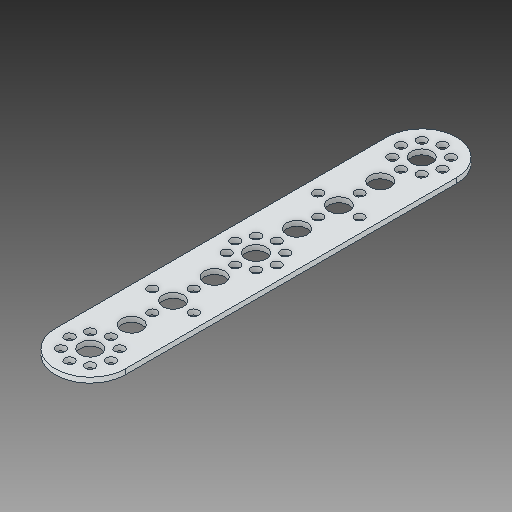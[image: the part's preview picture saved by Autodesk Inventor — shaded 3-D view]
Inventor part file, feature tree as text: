
AUTODESK INVENTOR PART (.ipt)
format: ipt  version: 2018 (Build 220112000, 112)  size: 172,032 bytes
history: native  units: in
note: dims shown in document units (in); Inventor stores cm internally (conversion verified against a paired STEP export)
features: extrude x1
ambient origin geometry x8: Origin, YZ Plane, XZ Plane, XY Plane, X Axis, Y Axis, Z Axis, Center Point
bodies: Solid1 (feature_tree)
feature tree (1):
  extrude  "Extrude2"  [1 undecoded]
note: 1 required parameter value undecoded (feature->parameter linkage not recoverable at this tier; creation-order binding heuristic only, values carry confidence <= 0.55)
